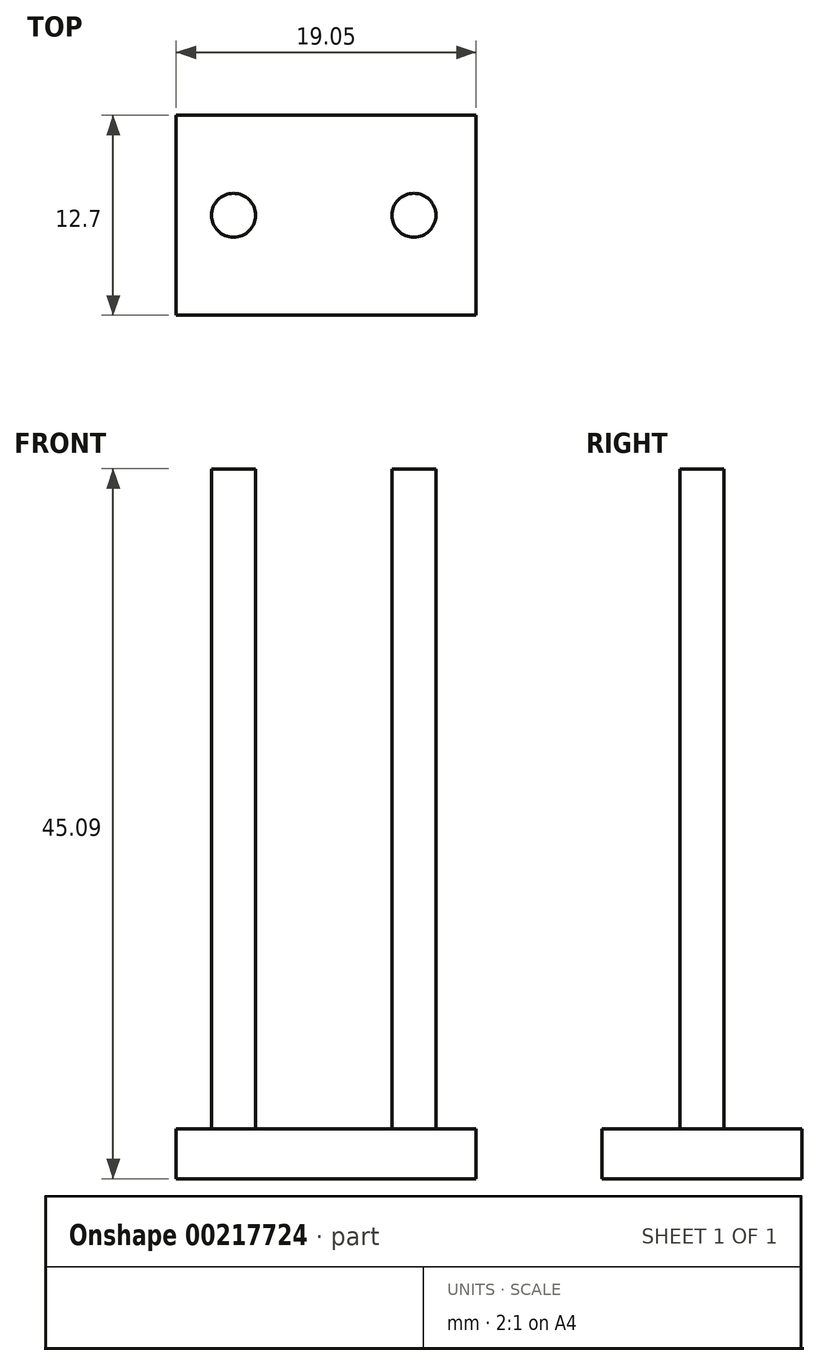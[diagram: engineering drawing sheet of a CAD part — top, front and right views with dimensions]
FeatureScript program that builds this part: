
annotation { "Feature Type Name" : "Feature", "Feature Type Description" : "" }
export const myFeature = defineFeature(function(context is Context, id is Id, definition is map)
    precondition{}
    {
        {
            var Q0;
            Q0=qCreatedBy(makeId("Top.planeOp"),FACE);
            var sketch = newSketch(context, id + "F0", { "sketchPlane" : qUnion([Q0])});
            skLineSegment(sketch, "E0.bottom", {"start": v(0, 0) * mm, "end": v(19.05, 0) * mm});
            skLineSegment(sketch, "E0.top", {"start": v(0, 12.7) * mm, "end": v(19.05, 12.7) * mm});
            skLineSegment(sketch, "E0.left", {"start": v(0, 0) * mm, "end": v(0, 12.7) * mm});
            skLineSegment(sketch, "E0.right", {"start": v(19.05, 0) * mm, "end": v(19.05, 12.7) * mm});
            skSolve(sketch);
        }
        {
            var Q0;
            Q0 = qSketchRegion(id + "F0", true);
            extrude(context, id + "F1", {"entities" : qUnion([Q0]), "depth" : 3.17 * mm});
        }
        {
            var Q0;
            Q0=makeQuery(id+"F1.opExtrude","CAP_FACE",FACE,{"disambiguationData":[OSD([sQuery(id+"F0.wireOp",EDGE,"E0.bottom"),sQuery(id+"F0.wireOp",EDGE,"E0.top"),sQuery(id+"F0.wireOp",EDGE,"E0.left"),sQuery(id+"F0.wireOp",EDGE,"E0.right")])],"isStart":false});
            var sketch = newSketch(context, id + "F2", { "sketchPlane" : qUnion([Q0])});
            skCircle(sketch, "E1", {"center": v(3.64, 6.35) * mm, "radius": 1.4 * mm});
            skLineSegment(sketch, "E2", {"start": v(3.64, 6.35) * mm, "end": v(15.1, 6.35) * mm});
            skCircle(sketch, "E3", {"center": v(15.1, 6.35) * mm, "radius": 1.4 * mm});
            skSolve(sketch);
        }
        {
            var Q0;
            Q0 = qSketchRegion(id + "F2", true);
            extrude(context, id + "F3", {"entities" : qUnion([Q0]), "operationType" : NewBodyOperationType.ADD, "depth" : 6.35 * mm});
        }
        {
            var Q0;
            Q0=makeQuery(id+"F3.opExtrude","CAP_FACE",FACE,{"disambiguationData":[OSD([sQuery(id+"F2.wireOp",EDGE,"E1")])],"isStart":false});
            var sketch = newSketch(context, id + "F4", { "sketchPlane" : qUnion([Q0])});
            skCircle(sketch, "E4", {"center": v(3.64, 6.35) * mm, "radius": 1.4 * mm});
            skLineSegment(sketch, "E5", {"start": v(3.64, 6.35) * mm, "end": v(15.1, 6.35) * mm});
            skCircle(sketch, "E6", {"center": v(15.1, 6.35) * mm, "radius": 1.4 * mm});
            skSolve(sketch);
        }
        {
            var Q0;
            Q0 = qSketchRegion(id + "F4", true);
            extrude(context, id + "F5", {"entities" : qUnion([Q0]), "operationType" : NewBodyOperationType.ADD, "depth" : 35.56 * mm});
        }
    });
